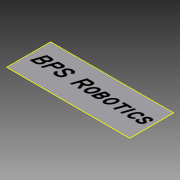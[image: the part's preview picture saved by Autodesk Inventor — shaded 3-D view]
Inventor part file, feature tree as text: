
AUTODESK INVENTOR PART (.ipt)
format: ipt  version: 2014 (Build 180170000, 170)  size: 75,264 bytes
history: native  units: in
note: dims shown in document units (in); Inventor stores cm internally (conversion verified against a paired STEP export)
features: sketch x2, extrude x1
ambient origin geometry x8: Origin, YZ Plane, XZ Plane, XY Plane, X Axis, Y Axis, Z Axis, Center Point
bodies: Solid1 (feature_tree)
feature tree (3):
  extrude  "Extrusion1"  Depth=30.0in
  sketch  "Sketch2"  dims[d2=0.1in d3=0.0in]
  sketch  "Sketch1"  dims[d0=84.0in d1=30.0in]
